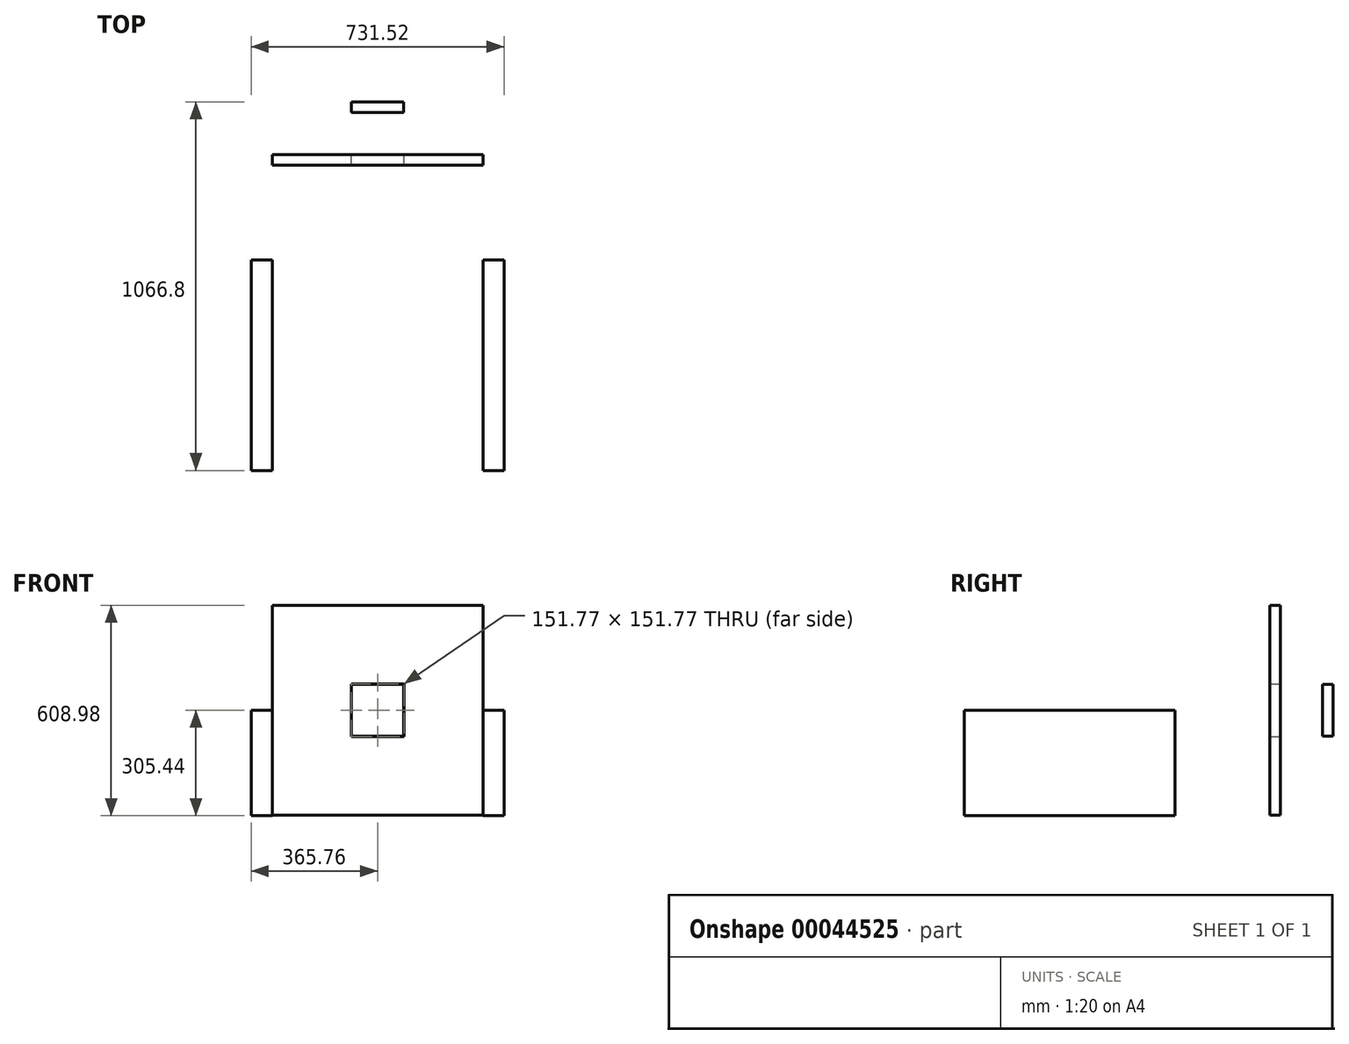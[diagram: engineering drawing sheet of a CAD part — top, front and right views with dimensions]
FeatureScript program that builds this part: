
annotation { "Feature Type Name" : "Feature", "Feature Type Description" : "" }
export const myFeature = defineFeature(function(context is Context, id is Id, definition is map)
    precondition{}
    {
        {
            var Q0;
            Q0=qCreatedBy(makeId("Front.planeOp"),FACE);
            cPlane(context, id + "F0", {"entities" : qUnion([Q0]), "cplaneType" : CPlaneType.OFFSET, "offset" : 914.4 * mm, "oppositeDirection" : true, "width" : 152.4 * mm, "height" : 152.4 * mm});
        }
        {
            var Q0;
            Q0=qCreatedBy(id+"F0.planeOp",FACE);
            var sketch = newSketch(context, id + "F1", { "sketchPlane" : qUnion([Q0])});
            skLineSegment(sketch, "E0.rect.bottom", {"start": v(-304.55, -303.54) * mm, "end": v(304.55, -303.54) * mm});
            skLineSegment(sketch, "E0.rect.top", {"start": v(-304.55, 303.54) * mm, "end": v(304.55, 303.54) * mm});
            skLineSegment(sketch, "E0.rect.left", {"start": v(-304.55, -303.54) * mm, "end": v(-304.55, 303.54) * mm});
            skLineSegment(sketch, "E0.rect.right", {"start": v(304.55, -303.54) * mm, "end": v(304.55, 303.54) * mm});
            skPoint(sketch, "E0.rect.middle", {"position": v(0, 0) * mm});
            skLineSegment(sketch, "E1.rect.bottom", {"start": v(-75.88, -75.89) * mm, "end": v(75.88, -75.89) * mm});
            skLineSegment(sketch, "E1.rect.top", {"start": v(-75.88, 75.89) * mm, "end": v(75.88, 75.89) * mm});
            skLineSegment(sketch, "E1.rect.left", {"start": v(-75.88, -75.89) * mm, "end": v(-75.88, 75.89) * mm});
            skLineSegment(sketch, "E1.rect.right", {"start": v(75.88, -75.89) * mm, "end": v(75.88, 75.89) * mm});
            skSolve(sketch);
        }
        {
            var Q0;
            Q0=makeQuery(id+"F1.imprint","IMPRINT",FACE,{"disambiguationData":[TD([[makeQuery(id+"F1.imprint","IMPRINT",EDGE,{"derivedFrom":sQuery(id+"F1.wireOp",EDGE,"E0.rect.bottom")}),1.0]])]});
            extrude(context, id + "F2", {"entities" : qUnion([Q0]), "depth" : 30.48 * mm});
        }
        {
            var Q0;
            Q0=qCreatedBy(makeId("Front.planeOp"),FACE);
            var sketch = newSketch(context, id + "F3", { "sketchPlane" : qUnion([Q0])});
            skLineSegment(sketch, "E2.rect.bottom", {"start": v(304.55, -194.27) * mm, "end": v(-304.55, -194.27) * mm});
            skLineSegment(sketch, "E2.rect.top", {"start": v(304.55, -254.97) * mm, "end": v(-304.55, -254.97) * mm});
            skLineSegment(sketch, "E2.rect.left", {"start": v(304.55, -194.27) * mm, "end": v(304.55, -254.97) * mm});
            skLineSegment(sketch, "E2.rect.right", {"start": v(-304.55, -194.27) * mm, "end": v(-304.55, -254.97) * mm});
            skPoint(sketch, "E2.rect.middle", {"position": v(0, -224.62) * mm});
            skSolve(sketch);
        }
        {
            var Q0;
            Q0=sQuery(id+"F3.wireOp",EDGE,"E2.rect.top");
            extrude(context, id + "F4", {"bodyType" : ToolBodyType.SURFACE, "surfaceEntities" : qUnion([Q0]), "oppositeDirection" : true, "depth" : 609.6 * mm});
        }
        {
            var Q0;
            Q0=sQuery(id+"F3.wireOp",EDGE,"E2.rect.bottom");
            extrude(context, id + "F5", {"bodyType" : ToolBodyType.SURFACE, "surfaceEntities" : qUnion([Q0]), "oppositeDirection" : true, "depth" : 609.6 * mm});
        }
        {
            var Q0;
            Q0=qCreatedBy(makeId("Front.planeOp"),FACE);
            var sketch = newSketch(context, id + "F6", { "sketchPlane" : qUnion([Q0])});
            skLineSegment(sketch, "E3", {"start": v(0, 0) * mm, "end": v(-304.8, 0) * mm});
            skLineSegment(sketch, "E4", {"start": v(0, 0) * mm, "end": v(304.8, 0) * mm});
            skLineSegment(sketch, "E5", {"start": v(-304.8, 0) * mm, "end": v(-304.8, -305.44) * mm});
            skLineSegment(sketch, "E6", {"start": v(-304.8, -305.44) * mm, "end": v(-304.8, 0) * mm});
            skLineSegment(sketch, "E7", {"start": v(304.8, 0) * mm, "end": v(304.8, -304.43) * mm});
            skLineSegment(sketch, "E8", {"start": v(-304.8, -305.44) * mm, "end": v(304.8, -305.44) * mm});
            skSolve(sketch);
        }
        {
            var Q0;
            Q0=sQuery(id+"F6.wireOp",EDGE,"E6");
            var Q1;
            Q1=sQuery(id+"F6.wireOp",EDGE,"E7");
            extrude(context, id + "F7", {"bodyType" : ToolBodyType.SURFACE, "surfaceEntities" : qUnion([Q0, Q1]), "oppositeDirection" : true, "depth" : 609.6 * mm});
        }
        {
            var Q0;
            Q0=makeQuery(id+"F7.opExtrude","SWEPT_FACE",FACE,{"disambiguationData":[OSD([sQuery(id+"F6.wireOp",EDGE,"E6")])]});
            extrude(context, id + "F8", {"entities" : qUnion([Q0]), "depth" : 30.48 * mm});
        }
        {
            var Q0;
            Q0=makeQuery(id+"F7.opExtrude","SWEPT_FACE",FACE,{"disambiguationData":[OSD([sQuery(id+"F6.wireOp",EDGE,"E7")])]});
            extrude(context, id + "F9", {"entities" : qUnion([Q0]), "depth" : 30.48 * mm});
        }
        {
            var Q0;
            Q0=sQuery(id+"F6.wireOp",EDGE,"E8");
            extrude(context, id + "F10", {"bodyType" : ToolBodyType.SURFACE, "surfaceEntities" : qUnion([Q0]), "oppositeDirection" : true, "depth" : 609.6 * mm});
        }
        {
            var Q0;
            Q0=makeQuery(id+"F1.imprint","IMPRINT",FACE,{"disambiguationData":[TD([[makeQuery(id+"F1.imprint","IMPRINT",EDGE,{"derivedFrom":sQuery(id+"F1.wireOp",EDGE,"E1.rect.bottom")}),1.0]])]});
            cPlane(context, id + "F11", {"entities" : qUnion([Q0]), "cplaneType" : CPlaneType.OFFSET, "offset" : 152.4 * mm, "oppositeDirection" : true, "width" : 152.4 * mm, "height" : 152.4 * mm});
        }
        {
            var Q0;
            Q0=qCreatedBy(id+"F11.planeOp",FACE);
            var sketch = newSketch(context, id + "F12", { "sketchPlane" : qUnion([Q0])});
            skLineSegment(sketch, "E9.rect.bottom", {"start": v(-75.33, -75.16) * mm, "end": v(75.33, -75.16) * mm});
            skLineSegment(sketch, "E9.rect.top", {"start": v(-75.33, 75.16) * mm, "end": v(75.33, 75.16) * mm});
            skLineSegment(sketch, "E9.rect.left", {"start": v(-75.33, -75.16) * mm, "end": v(-75.33, 75.16) * mm});
            skLineSegment(sketch, "E9.rect.right", {"start": v(75.33, -75.16) * mm, "end": v(75.33, 75.16) * mm});
            skPoint(sketch, "E9.rect.middle", {"position": v(0, 0) * mm});
            skSolve(sketch);
        }
        {
            var Q0;
            Q0=makeQuery(id+"F12.imprint","IMPRINT",FACE,{"disambiguationData":[TD([[makeQuery(id+"F12.imprint","IMPRINT",EDGE,{"derivedFrom":sQuery(id+"F12.wireOp",EDGE,"E9.rect.bottom")}),1.0]])]});
            extrude(context, id + "F13", {"entities" : qUnion([Q0]), "depth" : 30.48 * mm});
        }
        {
            var Q0;
            Q0=makeQuery(id+"F9.opExtrude","CAP_FACE",FACE,{"disambiguationData":[OSD([sQuery(id+"F6.wireOp",EDGE,"E7")])],"isStart":false});
            extrude(context, id + "F14", {"entities" : qUnion([Q0]), "operationType" : NewBodyOperationType.ADD, "depth" : 30.48 * mm});
        }
        {
            var Q0;
            Q0=makeQuery(id+"F8.opExtrude","CAP_FACE",FACE,{"disambiguationData":[OSD([sQuery(id+"F6.wireOp",EDGE,"E6")])],"isStart":false});
            extrude(context, id + "F15", {"entities" : qUnion([Q0]), "operationType" : NewBodyOperationType.ADD, "depth" : 30.48 * mm});
        }
    });
